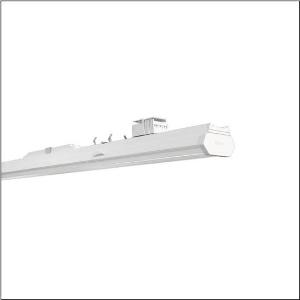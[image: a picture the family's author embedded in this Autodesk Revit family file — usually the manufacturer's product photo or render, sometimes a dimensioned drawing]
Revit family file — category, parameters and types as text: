
# Revit family: licross_21_protected_ho_52td12dn4dxm
name_source: partatom
category: Lighting Fixtures
units: mm (PartAtom-declared; Revit-internal decimal feet)

## family parameters
Cut with Voids When Loaded = No
Host = Face
Light Source = No
Part Type = Normal
Room Calculation Point = No
Round Connector Dimension = Use Diameter
Shared = No

## types (1)
- --- (1 x LED, 13000 lm, 74.3 W, 4000K)
    Apparent Load = 74 VA
    CIE Flux Codes = 70 91 97 98 100
    Color Rendering = 80
    Color Temperature = 4000K
    Default Elevation = 1800 mm
    Description = Licross 21 Protected HO, luminaire insert, of sheet steel, galvanised, coil coated, white, length: 1.500mm, width: 90mm, height: 103mm, LED rated luminous flux: 13.000lm, light colour: 840, SDCM (Standard Deviation of Colour Matching)MacAdam ≤ 3 SDCM (initial), control gear: DALI 2, with plug, 5-pole, with phase selection, mains connection: 220..240V, AC, 50/60Hz, rated input power: 74W, internal wiring halogen-free, primary light control with lens, of plastic, primary optical cover: cover, of PMMA, light emission: direct distribution, primary light characteristic: symmetric, protection rating (complete): IP54, insulation class (complete): insulation class I (protective earthing), certification: CE, ENEC, VDE, UKCA, protection symbol: D if used in an environment with non-conductive dust loads with corresponding accessories, impact resistance: IK06, permissible ambient temperature for indoor applications: -25..+40°C, corresponds to IFS (International Featured Standards) requirements for safety and quality in the food industry, reducing of maximum allowable ambient temperature of 5°C with ceiling mounting, LABS conformity tested according to VDMA 24364:2018-05, The light source and the operating device comply with the requirements of the Ecodesign Regulation (EU) 2019/2020 and are replaceable in accordance with this regulation, packaging unit: 1 piece
    Height = 92 mm
    Lamp = 1 x LED
    Lamp Light Flux = 13000 lm
    Lamp Power = 74.3 W
    Lamp count = 1
    Length = 1500 mm
    Luminous efficacy = 175 lm/W
    Manufacturer = Siteco
    ModVariant = No
    Model = 52TD12DN4DXM
    Mounting Place = Ceiling
    Mounting Type = Pendant
    Number of Poles = 1
    OnlyDefault = Yes
    Power Factor = 1
    Product Name = Licross 21 Protected HO
    Product group = luminaire insert | ceiling pendant
    ProductGroupID = 901
    Protection Class = Protection class I
    Protection Degree = IP 54
    RLX_Detail_Level = 1
    RLX_Emergency_Light_Flux = 0 lm
    RLX_Emergency_Type = 0
    RLX_Emergency_Type_DB = No
    RlxData = <blob elided: 24705 chars, md5=0cebe982>
    Socket = socket
    Standby Power = 0 W
    System Light Flux = 13000 lm
    System Power = 74 W
    Type Comments = factory setting: luminous flux: 100 % | dim-lin: 254 | 424 mA
    Type Image = l_1256148.jpg
    URL = http://relux.com
    VarID = @adj_130651
    Voltage = 0 V
    Weight = 0.00 kg
    Width = 88 mm

## geometry (parser evidence)
native form markers: Blend x4, Sweep x10
no freeform markers — native parametric forms only
